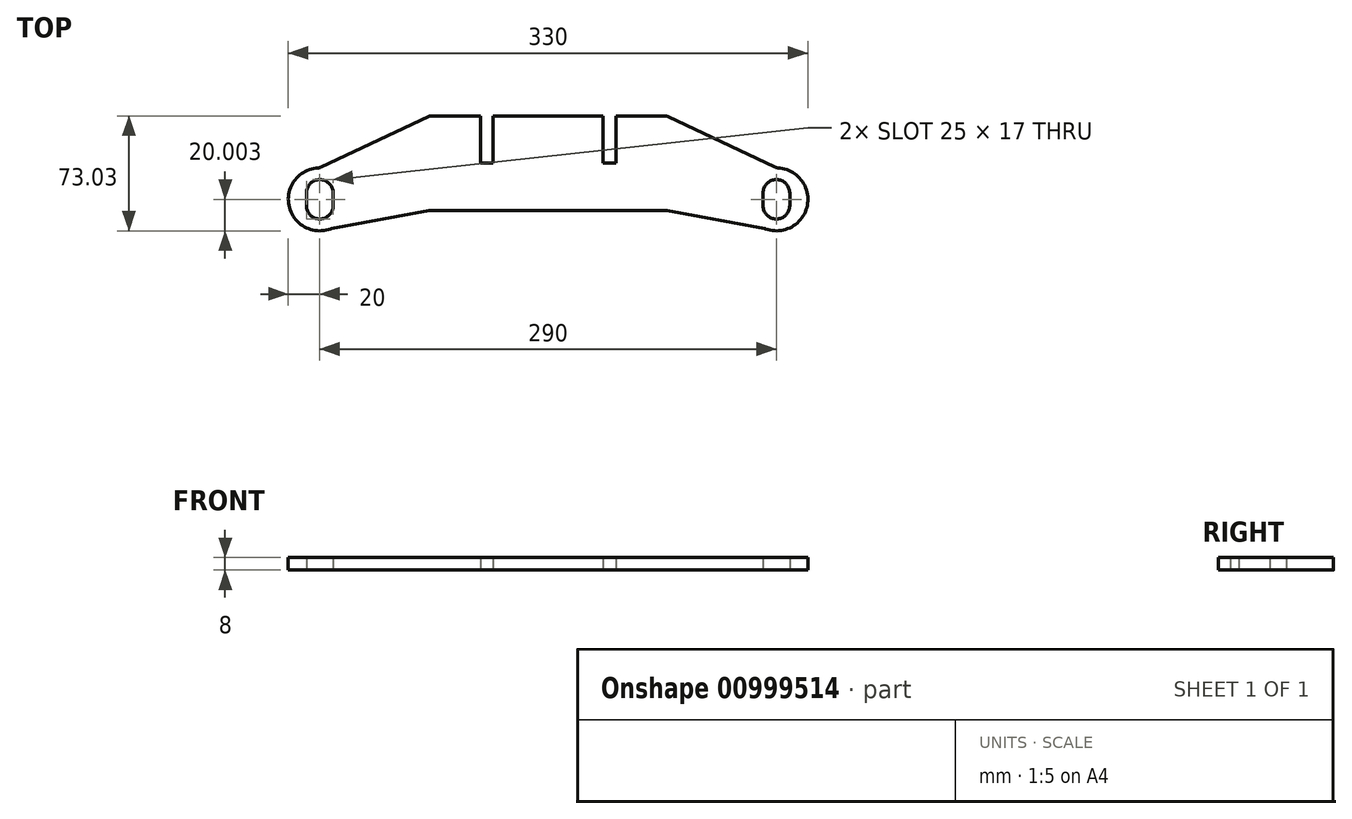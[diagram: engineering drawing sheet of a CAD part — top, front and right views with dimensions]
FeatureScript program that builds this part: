
annotation { "Feature Type Name" : "Feature", "Feature Type Description" : "" }
export const myFeature = defineFeature(function(context is Context, id is Id, definition is map)
    precondition{}
    {
        {
            var Q0;
            Q0=qCreatedBy(makeId("Top.planeOp"),FACE);
            var sketch = newSketch(context, id + "F0", { "sketchPlane" : qUnion([Q0])});
            skLineSegment(sketch, "E0.bottom", {"start": v(-75, -30) * mm, "end": v(75, -30) * mm});
            skLineSegment(sketch, "E0.top", {"start": v(-75, 30) * mm, "end": v(75, 30) * mm});
            skLineSegment(sketch, "E0.left", {"start": v(-75, -30) * mm, "end": v(-75, 30) * mm});
            skLineSegment(sketch, "E0.right", {"start": v(75, -30) * mm, "end": v(75, 30) * mm});
            skPoint(sketch, "E0.middle", {"position": v(0, 0) * mm});
            skLineSegment(sketch, "E1", {"start": v(-75, -30) * mm, "end": v(-145, -43.03) * mm});
            skLineSegment(sketch, "E2", {"start": v(75, -30) * mm, "end": v(145, -43.03) * mm});
            skLineSegment(sketch, "E3", {"start": v(75, 30) * mm, "end": v(145, -3.03) * mm});
            skLineSegment(sketch, "E4", {"start": v(-75, 30) * mm, "end": v(-145, -3.03) * mm});
            skLineSegment(sketch, "E5", {"start": v(-145, -3.03) * mm, "end": v(-145, -43.03) * mm});
            skLineSegment(sketch, "E6", {"start": v(145, -3.03) * mm, "end": v(145, -43.03) * mm});
            skCircle(sketch, "E7", {"center": v(-145, -23.03) * mm, "radius": 20 * mm});
            skCircle(sketch, "E8", {"center": v(145, -23.03) * mm, "radius": 20 * mm});
            skLineSegment(sketch, "E9.bottom", {"start": v(-153.5, -19.03) * mm, "end": v(-136.5, -19.03) * mm});
            skLineSegment(sketch, "E9.top", {"start": v(-153.5, -27.03) * mm, "end": v(-136.5, -27.03) * mm});
            skLineSegment(sketch, "E9.left", {"start": v(-153.5, -19.03) * mm, "end": v(-153.5, -27.03) * mm});
            skLineSegment(sketch, "E9.right", {"start": v(-136.5, -19.03) * mm, "end": v(-136.5, -27.03) * mm});
            skCircle(sketch, "E10", {"center": v(-145, -19.03) * mm, "radius": 8.5 * mm});
            skCircle(sketch, "E11", {"center": v(-145, -27.03) * mm, "radius": 8.5 * mm});
            skLineSegment(sketch, "E12.bottom", {"start": v(136.5, -19.03) * mm, "end": v(153.5, -19.03) * mm});
            skLineSegment(sketch, "E12.top", {"start": v(136.5, -27.03) * mm, "end": v(153.5, -27.03) * mm});
            skLineSegment(sketch, "E12.left", {"start": v(136.5, -19.03) * mm, "end": v(136.5, -27.03) * mm});
            skLineSegment(sketch, "E12.right", {"start": v(153.5, -19.03) * mm, "end": v(153.5, -27.03) * mm});
            skCircle(sketch, "E13", {"center": v(145, -19.03) * mm, "radius": 8.5 * mm});
            skCircle(sketch, "E14", {"center": v(145, -27.03) * mm, "radius": 8.5 * mm});
            skLineSegment(sketch, "E15.bottom", {"start": v(43, 30) * mm, "end": v(35, 30) * mm});
            skLineSegment(sketch, "E15.top", {"start": v(43, 0) * mm, "end": v(35, 0) * mm});
            skLineSegment(sketch, "E15.left", {"start": v(43, 30) * mm, "end": v(43, 0) * mm});
            skLineSegment(sketch, "E15.right", {"start": v(35, 30) * mm, "end": v(35, 0) * mm});
            skLineSegment(sketch, "E16.bottom", {"start": v(-35, 30) * mm, "end": v(-43, 30) * mm});
            skLineSegment(sketch, "E16.top", {"start": v(-35, 0) * mm, "end": v(-43, 0) * mm});
            skLineSegment(sketch, "E16.left", {"start": v(-35, 30) * mm, "end": v(-35, 0) * mm});
            skLineSegment(sketch, "E16.right", {"start": v(-43, 30) * mm, "end": v(-43, 0) * mm});
            skLineSegment(sketch, "E17", {"start": v(-145, -23.03) * mm, "end": v(-145, -53.03) * mm});
            skLineSegment(sketch, "E18", {"start": v(-66.32, -30) * mm, "end": v(-66.32, -53) * mm});
            skSolve(sketch);
        }
        {
            var Q0;
            {var subQ0=sQuery(id+"F0.wireOp",EDGE,"E7");var subQ1=sQuery(id+"F0.wireOp",EDGE,"E1");var subQ3=makeQuery(id+"F0.imprint","INTERSECT",VERTEX,{"derivedFrom":[subQ1,subQ0]});Q0=makeQuery(id+"F0.imprint","IMPRINT",FACE,{"disambiguationData":[TD([[makeQuery(id+"F0.imprint","IMPRINT",EDGE,{"disambiguationData":[TD([[subQ3,-1.0]])],"derivedFrom":subQ1}),1.0]])]});}
            var Q1;
            {var subQ0=sQuery(id+"F0.wireOp",EDGE,"E8");var subQ1=sQuery(id+"F0.wireOp",EDGE,"E2");var subQ3=makeQuery(id+"F0.imprint","INTERSECT",VERTEX,{"derivedFrom":[subQ1,subQ0]});Q1=makeQuery(id+"F0.imprint","IMPRINT",FACE,{"disambiguationData":[TD([[makeQuery(id+"F0.imprint","IMPRINT",EDGE,{"disambiguationData":[TD([[subQ3,-1.0]])],"derivedFrom":subQ1}),-1.0]])]});}
            var Q2;
            {var subQ0=sQuery(id+"F0.wireOp",EDGE,"E0.left");Q2=makeQuery(id+"F0.imprint","IMPRINT",FACE,{"disambiguationData":[TD([[makeQuery(id+"F0.imprint","IMPRINT",EDGE,{"derivedFrom":subQ0}),1.0]])]});}
            var Q3;
            {var subQ0=sQuery(id+"F0.wireOp",EDGE,"E0.right");Q3=makeQuery(id+"F0.imprint","IMPRINT",FACE,{"disambiguationData":[TD([[makeQuery(id+"F0.imprint","IMPRINT",EDGE,{"derivedFrom":subQ0}),-1.0]])]});}
            var Q4;
            Q4=makeQuery(id+"F0.imprint","IMPRINT",FACE,{"disambiguationData":[TD([[makeQuery(id+"F0.imprint","IMPRINT",EDGE,{"derivedFrom":sQuery(id+"F0.wireOp",EDGE,"E0.top")}),-1.0]])]});
            var Q5;
            {var subQ4=sQuery(id+"F0.wireOp",EDGE,"E9.left");Q5=makeQuery(id+"F0.imprint","IMPRINT",FACE,{"disambiguationData":[TD([[makeQuery(id+"F0.imprint","IMPRINT",EDGE,{"derivedFrom":subQ4}),-1.0]])]});}
            var Q6;
            {var subQ4=sQuery(id+"F0.wireOp",EDGE,"E12.right");Q6=makeQuery(id+"F0.imprint","IMPRINT",FACE,{"disambiguationData":[TD([[makeQuery(id+"F0.imprint","IMPRINT",EDGE,{"derivedFrom":subQ4}),1.0]])]});}
            var Q7;
            {var subQ6=sQuery(id+"F0.wireOp",EDGE,"E9.right");Q7=makeQuery(id+"F0.imprint","IMPRINT",FACE,{"disambiguationData":[TD([[makeQuery(id+"F0.imprint","IMPRINT",EDGE,{"derivedFrom":subQ6}),1.0]])]});}
            var Q8;
            {var subQ10=sQuery(id+"F0.wireOp",EDGE,"E12.left");Q8=makeQuery(id+"F0.imprint","IMPRINT",FACE,{"disambiguationData":[TD([[makeQuery(id+"F0.imprint","IMPRINT",EDGE,{"derivedFrom":subQ10}),-1.0]])]});}
            extrude(context, id + "F1", {"entities" : qUnion([Q0, Q1, Q2, Q3, Q4, Q5, Q6, Q7, Q8]), "depth" : 8 * mm, "offsetDistance" : 25 * mm});
        }
        {
            var Q0;
            Q0=makeQuery(id+"F1.opExtrude","SWEPT_EDGE",EDGE,{"disambiguationData":[OSD([sQuery(id+"F0.wireOp",EDGE,"E0.bottom"),sQuery(id+"F0.wireOp",EDGE,"E0.right"),sQuery(id+"F0.wireOp",EDGE,"E2")])]});
            var Q1;
            Q1=makeQuery(id+"F1.opExtrude","SWEPT_EDGE",EDGE,{"disambiguationData":[OSD([sQuery(id+"F0.wireOp",EDGE,"E0.bottom"),sQuery(id+"F0.wireOp",EDGE,"E0.left"),sQuery(id+"F0.wireOp",EDGE,"E1")])]});
            var Q2;
            Q2=makeQuery(id+"F1.opExtrude","SWEPT_EDGE",EDGE,{"disambiguationData":[OSD([sQuery(id+"F0.wireOp",EDGE,"E0.top"),sQuery(id+"F0.wireOp",EDGE,"E0.left"),sQuery(id+"F0.wireOp",EDGE,"E4")])]});
            var Q3;
            Q3=makeQuery(id+"F1.opExtrude","SWEPT_EDGE",EDGE,{"disambiguationData":[OSD([sQuery(id+"F0.wireOp",EDGE,"E0.top"),sQuery(id+"F0.wireOp",EDGE,"E0.right"),sQuery(id+"F0.wireOp",EDGE,"E3")])]});
            var Q4;
            Q4=makeQuery(id+"F1.opExtrude","SWEPT_EDGE",EDGE,{"disambiguationData":[OSD([sQuery(id+"F0.wireOp",EDGE,"E3"),sQuery(id+"F0.wireOp",EDGE,"E6"),sQuery(id+"F0.wireOp",EDGE,"E8")])]});
            var Q5;
            Q5=makeQuery(id+"F1.opExtrude","SWEPT_EDGE",EDGE,{"disambiguationData":[OSD([sQuery(id+"F0.wireOp",EDGE,"E4"),sQuery(id+"F0.wireOp",EDGE,"E5"),sQuery(id+"F0.wireOp",EDGE,"E7")])]});
            var Q6;
            Q6=makeQuery(id+"F1.opExtrude","SWEPT_EDGE",EDGE,{"disambiguationData":[OSD([sQuery(id+"F0.wireOp",EDGE,"E1"),sQuery(id+"F0.wireOp",EDGE,"E7")])]});
            var Q7;
            Q7=makeQuery(id+"F1.opExtrude","SWEPT_EDGE",EDGE,{"disambiguationData":[OSD([sQuery(id+"F0.wireOp",EDGE,"E2"),sQuery(id+"F0.wireOp",EDGE,"E8")])]});
            fillet(context, id + "F2", {"entities" : qUnion([Q0, Q1, Q2, Q3, Q4, Q5, Q6, Q7]), "radius" : 5 * mm, "tangentPropagation" : true, "allowEdgeOverflow" : false});
        }
    });
